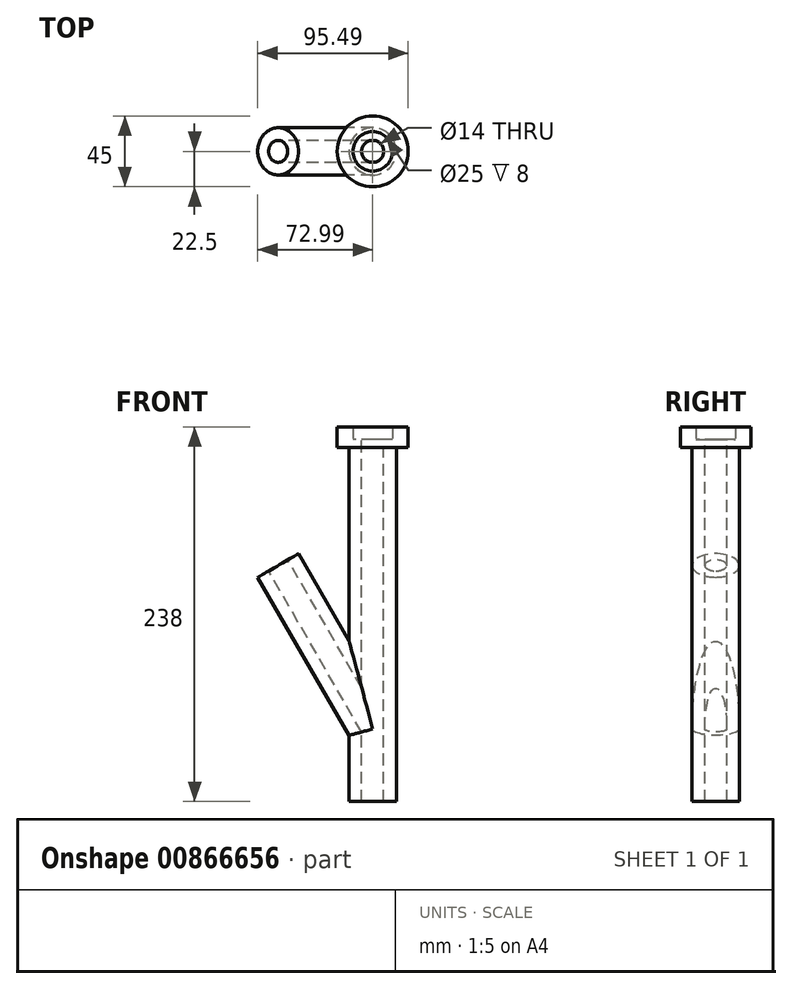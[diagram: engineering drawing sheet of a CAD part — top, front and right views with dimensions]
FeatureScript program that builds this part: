
annotation { "Feature Type Name" : "Feature", "Feature Type Description" : "" }
export const myFeature = defineFeature(function(context is Context, id is Id, definition is map)
    precondition{}
    {
        {
            var Q0;
            Q0=qCreatedBy(makeId("Top.planeOp"),FACE);
            var sketch = newSketch(context, id + "F0", { "sketchPlane" : qUnion([Q0])});
            skLineSegment(sketch, "E0", {"start": v(-60, -41.16) * mm, "end": v(-60, 117.75) * mm});
            skSolve(sketch);
        }
        {
            var Q0;
            Q0=sQuery(id+"F0.wireOp",EDGE,"E0");
            cPlane(context, id + "F1", {"entities" : qUnion([Q0]), "cplaneType" : CPlaneType.LINE_ANGLE, "offset" : 25 * mm, "angle" : 150 * degree, "width" : 150 * mm, "height" : 150 * mm});
        }
        {
            var Q0;
            Q0=qCreatedBy(id+"F1.planeOp",FACE);
            var sketch = newSketch(context, id + "F2", { "sketchPlane" : qUnion([Q0])});
            skCircle(sketch, "E1", {"center": v(-51.96, 0) * mm, "radius": 15 * mm});
            skSolve(sketch);
        }
        {
            var Q0;
            Q0=makeQuery(id+"F2.imprint","IMPRINT",FACE,{"disambiguationData":[TD([[makeQuery(id+"F2.imprint","IMPRINT",EDGE,{"derivedFrom":sQuery(id+"F2.wireOp",EDGE,"E1")}),1.0]])]});
            var Q1;
            Q1=qCreatedBy(makeId("Right.planeOp"),FACE);
            extrude(context, id + "F3", {"entities" : qUnion([Q0]), "endBound" : BoundingType.UP_TO_SURFACE, "depth" : 25 * mm, "endBoundEntityFace" : qUnion([Q1]), "offsetDistance" : 25 * mm});
        }
        {
            var Q0;
            Q0=qCreatedBy(makeId("Top.planeOp"),FACE);
            var sketch = newSketch(context, id + "F4", { "sketchPlane" : qUnion([Q0])});
            skCircle(sketch, "E2", {"center": v(0, 0) * mm, "radius": 15 * mm});
            skSolve(sketch);
        }
        {
            var Q0;
            Q0=makeQuery(id+"F4.imprint","IMPRINT",FACE,{"disambiguationData":[TD([[makeQuery(id+"F4.imprint","IMPRINT",EDGE,{"derivedFrom":sQuery(id+"F4.wireOp",EDGE,"E2")}),1.0]])]});
            extrude(context, id + "F5", {"entities" : qUnion([Q0]), "operationType" : NewBodyOperationType.ADD, "depth" : 80 * mm, "offsetDistance" : 25 * mm, "hasSecondDirection" : true, "secondDirectionOppositeDirection" : true, "secondDirectionDepth" : 150 * mm});
        }
        {
            var Q0;
            Q0=qCreatedBy(id+"F1.planeOp",FACE);
            var sketch = newSketch(context, id + "F6", { "sketchPlane" : qUnion([Q0])});
            skCircle(sketch, "E3", {"center": v(-51.96, 0) * mm, "radius": 7 * mm});
            skSolve(sketch);
        }
        {
            var Q0;
            Q0 = qSketchRegion(id + "F6", true);
            var Q1;
            Q1=qCreatedBy(makeId("Right.planeOp"),FACE);
            extrude(context, id + "F7", {"entities" : qUnion([Q0]), "operationType" : NewBodyOperationType.REMOVE, "endBound" : BoundingType.UP_TO_SURFACE, "depth" : 25 * mm, "endBoundEntityFace" : qUnion([Q1]), "offsetDistance" : 25 * mm});
        }
        {
            var Q0;
            Q0=makeQuery(id+"F5.opExtrude","CAP_FACE",FACE,{"disambiguationData":[OSD([sQuery(id+"F4.wireOp",EDGE,"E2")])],"isStart":false});
            var sketch = newSketch(context, id + "F8", { "sketchPlane" : qUnion([Q0])});
            skCircle(sketch, "E4", {"center": v(0, 0) * mm, "radius": 7 * mm});
            skSolve(sketch);
        }
        {
            var Q0;
            Q0=makeQuery(id+"F8.imprint","IMPRINT",FACE,{"disambiguationData":[TD([[makeQuery(id+"F8.imprint","IMPRINT",EDGE,{"derivedFrom":sQuery(id+"F8.wireOp",EDGE,"E4")}),1.0]])]});
            extrude(context, id + "F9", {"entities" : qUnion([Q0]), "operationType" : NewBodyOperationType.REMOVE, "endBound" : BoundingType.THROUGH_ALL, "oppositeDirection" : true, "depth" : 25 * mm, "offsetDistance" : 25 * mm});
        }
        {
            var Q0;
            Q0=makeQuery(id+"F5.opExtrude","CAP_FACE",FACE,{"disambiguationData":[OSD([sQuery(id+"F4.wireOp",EDGE,"E2")])],"isStart":false});
            var sketch = newSketch(context, id + "F10", { "sketchPlane" : qUnion([Q0])});
            skSolve(sketch);
        }
        {
            var Q0;
            Q0=makeQuery(id+"F10.imprint","IMPRINT",FACE,{"disambiguationData":[TD([[makeQuery(id+"F10.imprint","IMPRINT",EDGE,{"derivedFrom":makeQuery(id+"F5.opExtrude","CAP_EDGE",EDGE,{"disambiguationData":[OSD([sQuery(id+"F4.wireOp",EDGE,"E2")])],"isStart":false})}),1.0]])]});
            var sketch = newSketch(context, id + "F11", { "sketchPlane" : qUnion([Q0])});
            skCircle(sketch, "E5", {"center": v(0, 0) * mm, "radius": 22.5 * mm});
            skCircle(sketch, "E6", {"center": v(0, 0) * mm, "radius": 12.5 * mm});
            skSolve(sketch);
        }
        {
            var Q0;
            Q0=makeQuery(id+"F11.imprint","IMPRINT",FACE,{"disambiguationData":[TD([[makeQuery(id+"F11.imprint","IMPRINT",EDGE,{"derivedFrom":sQuery(id+"F11.wireOp",EDGE,"E5")}),1.0]])]});
            var Q1;
            Q1=makeQuery(id+"F11.imprint","IMPRINT",FACE,{"disambiguationData":[TD([[makeQuery(id+"F11.imprint","IMPRINT",EDGE,{"derivedFrom":sQuery(id+"F11.wireOp",EDGE,"E6")}),-1.0]])]});
            extrude(context, id + "F12", {"entities" : qUnion([Q0, Q1]), "operationType" : NewBodyOperationType.ADD, "depth" : 8 * mm, "offsetDistance" : 25 * mm, "hasSecondDirection" : true, "secondDirectionOppositeDirection" : true, "secondDirectionDepth" : 5 * mm});
        }
    });
